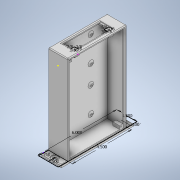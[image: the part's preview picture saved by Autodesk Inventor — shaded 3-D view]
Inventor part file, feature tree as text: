
AUTODESK INVENTOR PART (.ipt)
format: ipt  version: 2020 (Build 240168000, 168)  size: 448,512 bytes
history: native  units: in
note: dims shown in document units (in); Inventor stores cm internally (conversion verified against a paired STEP export)
features: sketch x13, extrude x12, hole x4, fillet x4, pattern_linear x2, thread x1
ambient origin geometry x8: Origin, YZ Plane, XZ Plane, XY Plane, X Axis, Y Axis, Z Axis, Center Point
bodies: Solid1 (feature_tree)
feature tree (36):
  sketch  "Sketch1"  dims[d0=1.5in d1=6.0in]
  extrude  "Extrusion1"  Depth=6.0in
  extrude  "Extrusion2"  Depth=0.75in
  hole  "Hole1"  [1 undecoded]
  extrude  "Extrusion7"  Depth=0.1875in
  extrude  "Extrusion8"  Depth=0.1875in
  extrude  "Extrusion3"  Depth=0.125in
  extrude  "Extrusion4"  Depth=0.125in
  extrude  "Extrusion5"  Depth=0.125in TaperAngle=0.0deg
  extrude  "Extrusion6"  Depth=0.25in
  extrude  "Extrusion9"  Depth=0.5in
  hole  "Hole2"  [1 undecoded]
  thread  "Thread1"  [1 undecoded]
  pattern_linear  "Rectangular Pattern1"  Spacing1=1.9291in  [1 undecoded]
  hole  "Hole4"  [1 undecoded]
  fillet  "Fillet1"  Radius=0.25in
  extrude  "Extrusion11"  Depth=0.5in
  extrude  "Extrusion12"  Depth=0.25in TaperAngle=0.0deg
  sketch  "Sketch18"  dims[d36=0.9252in d37=1.9291in d38=2.2835in d39=0.25in d40=0.0in d41=0.5in d43=0.25in d44=0.0in d45=0.1969in d46=0.0787in d47=0.0in d48=0.0807in d49=0.197in d50=0.119in d51=0.188in d52=90.0deg d53=0.25in d54=0.8108in d55=0.25in d56=0.0in d57=0.7874in d59=2.2835in d60=0.7874in d62=1.9291in d82=0.1875in d83=0.1875in d84=0.125in d85=0.125in d86=0.089in d87=0.146in d88=0.119in d89=0.188in d90=0.5635in d91=0.224in d92=0.8108in d93=0.0625in d128=2.75in d130=0.75in d131=0.0in d132=1.0in d133=3.0in d134=0.0625in d135=0.0in d136=1.5in d137=0.5in d138=90.0deg d139=0.75in d140=2.75in d141=0.125in d142=0.0in d143=0.375in d144=0.375in d145=0.375in d146=0.375in d147=0.375in d148=0.0in d149=0.1875in d150=0.1875in d151=0.1875in d152=0.1875in d153=0.089in d154=0.197in d155=0.119in d156=0.188in d157=0.5635in d158=0.259in d159=0.8108in d160=0.0625in d198=0.125in d206=0.3779in d224=0.3779in d244=0.3779in d262=0.3779in d273=0.7874in d275=3.3465in d276=0.125in]
  extrude  "Extrusion13"  Depth=0.125in
  hole  "Hole6"  [1 undecoded]
  fillet  "Fillet2"  Radius=0.1875in
  fillet  "Fillet3"  Radius=0.1875in
  pattern_linear  "Rectangular Pattern3"  Spacing1=0.125in  [1 undecoded]
  fillet  "Fillet4"  Radius=0.125in
  sketch  "Sketch2"  dims[d2=0.75in d3=4.5in]
  sketch  "Sketch3"  dims[d4=0.1875in d5=0.0in d6=6.75in d7=0.0in]
  sketch  "Sketch4"  dims[d8=0.5in]
  sketch  "Sketch5"  dims[d9=0.266in d10=0.75in d11=0.507in d12=0.0625in d13=0.5635in d14=1.0in d15=0.8108in d16=0.1875in]
  sketch  "Sketch6"  dims[d17=0.1875in d18=0.1875in]
  sketch  "Sketch7"  dims[d19=1.3125in d20=0.0in d21=0.125in]
  sketch  "Sketch8"  dims[d22=0.125in d23=0.125in]
  sketch  "Sketch9"  dims[d24=0.125in d25=0.125in d26=0.0in]
  sketch  "Sketch12"  dims[d27=0.5in d28=0.25in]
  sketch  "Sketch16"  dims[d29=0.25in d30=0.0in d31=0.5in]
  sketch  "Sketch17"  dims[d32=0.25in d33=0.25in d34=0.0in d35=0.5906in]
note: 7 required parameter values undecoded (feature->parameter linkage not recoverable at this tier; creation-order binding heuristic only, values carry confidence <= 0.55)
